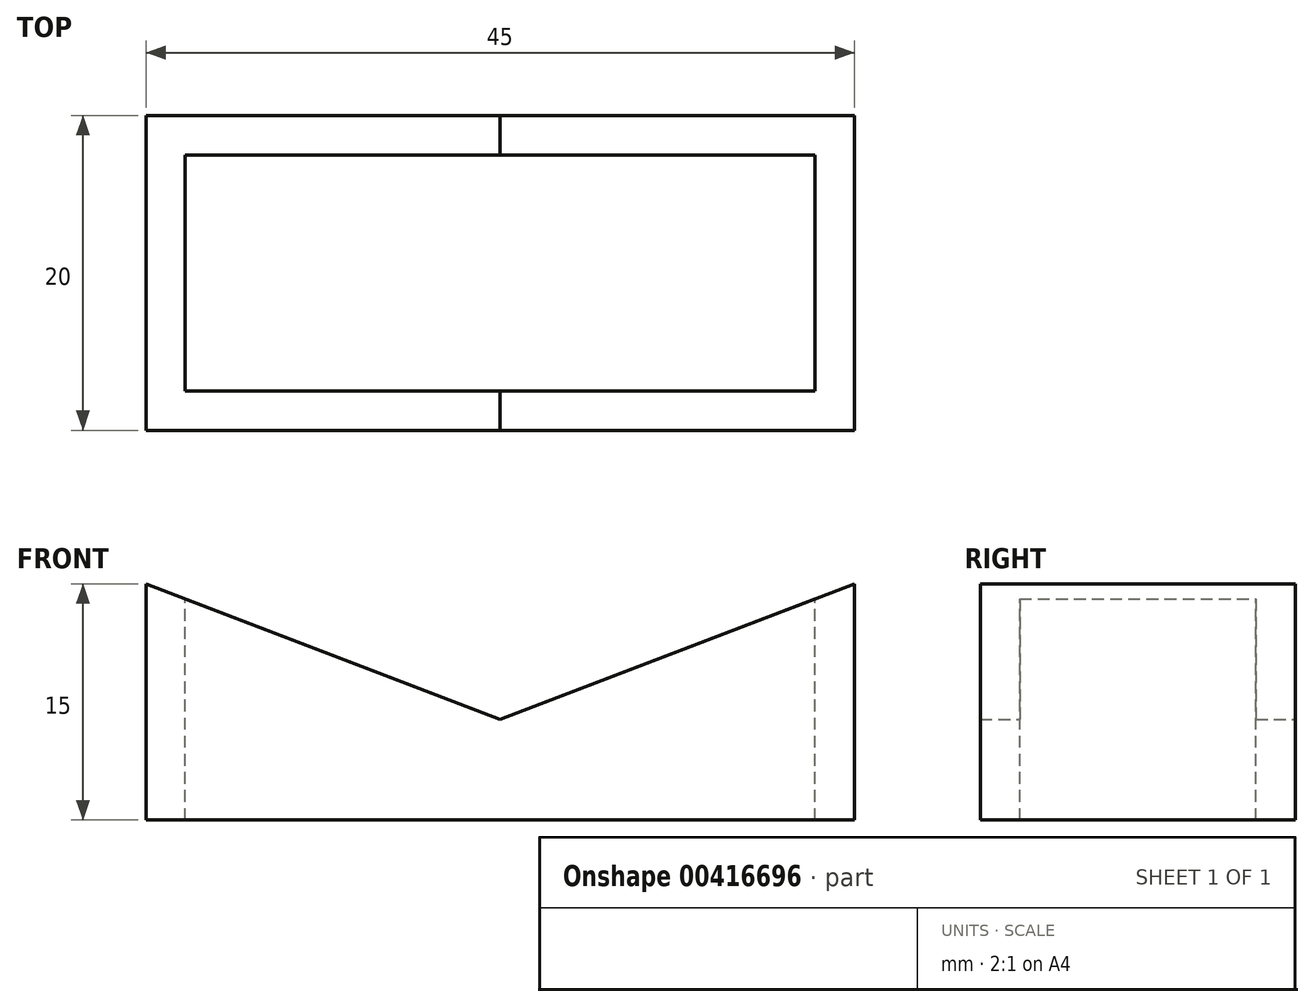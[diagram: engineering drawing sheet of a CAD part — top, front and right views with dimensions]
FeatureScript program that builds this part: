
annotation { "Feature Type Name" : "Feature", "Feature Type Description" : "" }
export const myFeature = defineFeature(function(context is Context, id is Id, definition is map)
    precondition{}
    {
        {
            var Q0;
            Q0=qCreatedBy(makeId("Front.planeOp"),FACE);
            var sketch = newSketch(context, id + "F0", { "sketchPlane" : qUnion([Q0])});
            skLineSegment(sketch, "E0.bottom", {"start": v(-22.5, 0) * mm, "end": v(22.5, 0) * mm});
            skLineSegment(sketch, "E0.left", {"start": v(-22.5, 0) * mm, "end": v(-22.5, 15) * mm});
            skLineSegment(sketch, "E0.right", {"start": v(22.5, 0) * mm, "end": v(22.5, 15) * mm});
            skPoint(sketch, "E1", {"position": v(0, 6.4) * mm});
            skLineSegment(sketch, "E2", {"start": v(-22.5, 15) * mm, "end": v(0, 6.4) * mm});
            skLineSegment(sketch, "E3", {"start": v(0, 6.4) * mm, "end": v(22.5, 15) * mm});
            skSolve(sketch);
        }
        {
            var Q0;
            Q0=makeQuery(id+"F0.imprint","IMPRINT",FACE,{"disambiguationData":[TD([[makeQuery(id+"F0.imprint","IMPRINT",EDGE,{"derivedFrom":sQuery(id+"F0.wireOp",EDGE,"E0.bottom")}),1.0]])]});
            extrude(context, id + "F1", {"entities" : qUnion([Q0]), "depth" : 10 * mm, "hasSecondDirection" : true, "secondDirectionOppositeDirection" : true, "secondDirectionDepth" : 10 * mm});
        }
        {
            var Q0;
            Q0=makeQuery(id+"F1.opExtrude","SWEPT_FACE",FACE,{"disambiguationData":[OSD([sQuery(id+"F0.wireOp",EDGE,"E0.bottom")])]});
            var Q1;
            Q1=makeQuery(id+"F1.opExtrude","SWEPT_FACE",FACE,{"disambiguationData":[OSD([sQuery(id+"F0.wireOp",EDGE,"E2")])]});
            var Q2;
            Q2=makeQuery(id+"F1.opExtrude","SWEPT_FACE",FACE,{"disambiguationData":[OSD([sQuery(id+"F0.wireOp",EDGE,"E3")])]});
            shell(context, id + "F2", {"entities" : qUnion([Q0, Q1, Q2]), "thickness" : 2.5 * mm});
        }
    });
